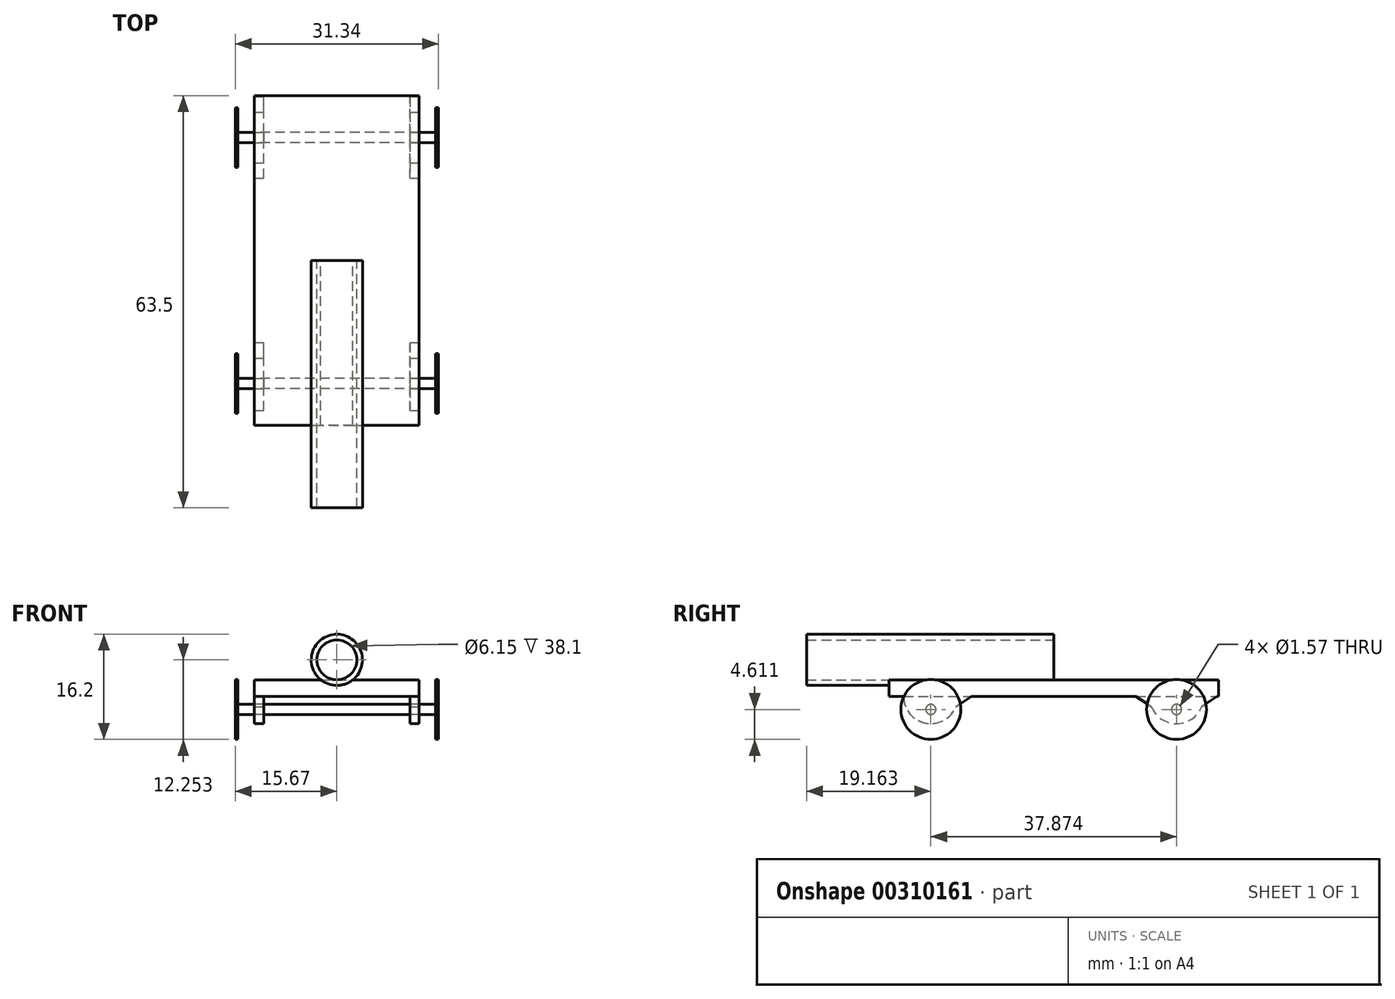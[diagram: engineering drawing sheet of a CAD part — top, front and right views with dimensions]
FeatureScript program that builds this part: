
annotation { "Feature Type Name" : "Feature", "Feature Type Description" : "" }
export const myFeature = defineFeature(function(context is Context, id is Id, definition is map)
    precondition{}
    {
        {
            var Q0;
            Q0=qCreatedBy(makeId("Top.planeOp"),FACE);
            var sketch = newSketch(context, id + "F0", { "sketchPlane" : qUnion([Q0])});
            skLineSegment(sketch, "E0", {"start": v(-12.7, 25.4) * mm, "end": v(-12.7, -25.4) * mm});
            skLineSegment(sketch, "E1", {"start": v(-12.7, -25.4) * mm, "end": v(12.7, -25.4) * mm});
            skLineSegment(sketch, "E2", {"start": v(12.7, -25.4) * mm, "end": v(12.7, 25.4) * mm});
            skLineSegment(sketch, "E3", {"start": v(12.7, 25.4) * mm, "end": v(-12.7, 25.4) * mm});
            skLineSegment(sketch, "E4", {"start": v(0, 25.4) * mm, "end": v(0, -25.4) * mm, "construction": true});
            skSolve(sketch);
        }
        {
            var Q0;
            Q0=makeQuery(id+"F0.imprint","IMPRINT",FACE,{"disambiguationData":[TD([[makeQuery(id+"F0.imprint","IMPRINT",EDGE,{"derivedFrom":sQuery(id+"F0.wireOp",EDGE,"E0")}),1.0]])]});
            extrude(context, id + "F1", {"entities" : qUnion([Q0]), "depth" : 2.54 * mm});
        }
        {
            var Q0;
            Q0=makeQuery(id+"F1.opExtrude","SWEPT_FACE",FACE,{"disambiguationData":[OSD([sQuery(id+"F0.wireOp",EDGE,"E1")])]});
            var sketch = newSketch(context, id + "F2", { "sketchPlane" : qUnion([Q0])});
            skCircle(sketch, "E5", {"center": v(0, 5.61) * mm, "radius": 3.07 * mm});
            skCircle(sketch, "E6", {"center": v(0, 5.61) * mm, "radius": 3.95 * mm});
            skSolve(sketch);
        }
        {
            var Q0;
            {var subQ0=sQuery(id+"F2.wireOp",EDGE,"E5");Q0=makeQuery(id+"F2.imprint","IMPRINT",FACE,{"disambiguationData":[TD([[makeQuery(id+"F2.imprint","IMPRINT",EDGE,{"derivedFrom":subQ0}),-1.0]])]});}
            var Q1;
            {var subQ0=sQuery(id+"F2.wireOp",EDGE,"E6");var subQ1=makeQuery(id+"F1.opExtrude","CAP_EDGE",EDGE,{"disambiguationData":[OSD([sQuery(id+"F0.wireOp",EDGE,"E1")])],"isStart":false});var subQ2=makeQuery(id+"F2.imprint","INTERSECT",VERTEX,{"disambiguationData":[OD(0.0)],"derivedFrom":[subQ1,subQ0]});Q1=makeQuery(id+"F2.imprint","IMPRINT",FACE,{"disambiguationData":[TD([[makeQuery(id+"F2.imprint","IMPRINT",EDGE,{"disambiguationData":[TD([[subQ2,-1.0]])],"derivedFrom":subQ0}),1.0]])]});}
            extrude(context, id + "F3", {"entities" : qUnion([Q0, Q1]), "operationType" : NewBodyOperationType.ADD, "depth" : 12.7 * mm, "hasSecondDirection" : true, "secondDirectionOppositeDirection" : true, "secondDirectionDepth" : 25.4 * mm});
        }
        {
            var Q0;
            Q0=makeQuery(id+"F1.opExtrude","SWEPT_FACE",FACE,{"disambiguationData":[OSD([sQuery(id+"F0.wireOp",EDGE,"E2")])]});
            var sketch = newSketch(context, id + "F4", { "sketchPlane" : qUnion([Q0])});
            skCircle(sketch, "E7", {"center": v(-18.94, 0) * mm, "radius": 4.21 * mm});
            skCircle(sketch, "E8", {"center": v(18.94, 0) * mm, "radius": 4.21 * mm});
            skLineSegment(sketch, "E9", {"start": v(0, 0) * mm, "end": v(-18.94, 0) * mm, "construction": true});
            skLineSegment(sketch, "E10", {"start": v(0, 0) * mm, "end": v(18.94, 0) * mm, "construction": true});
            skCircle(sketch, "E11", {"center": v(-18.94, -2.03) * mm, "radius": 0.78 * mm});
            skCircle(sketch, "E12", {"center": v(18.94, -2.03) * mm, "radius": 0.78 * mm});
            skLineSegment(sketch, "E13", {"start": v(-18.94, 0) * mm, "end": v(-18.94, -2.03) * mm, "construction": true});
            skLineSegment(sketch, "E14", {"start": v(18.94, 0) * mm, "end": v(18.94, -2.03) * mm, "construction": true});
            skSolve(sketch);
        }
        {
            var Q0;
            {var subQ0=sQuery(id+"F4.wireOp",EDGE,"E7");var subQ1=makeQuery(id+"F1.opExtrude","CAP_EDGE",EDGE,{"disambiguationData":[OSD([sQuery(id+"F0.wireOp",EDGE,"E2")])],"isStart":true});var subQ2=makeQuery(id+"F4.imprint","INTERSECT",VERTEX,{"disambiguationData":[OD(0.0)],"derivedFrom":[subQ1,subQ0]});Q0=makeQuery(id+"F4.imprint","IMPRINT",FACE,{"disambiguationData":[TD([[makeQuery(id+"F4.imprint","IMPRINT",EDGE,{"disambiguationData":[TD([[subQ2,1.0]])],"derivedFrom":subQ0}),1.0]])]});}
            var Q1;
            {var subQ0=sQuery(id+"F4.wireOp",EDGE,"E8");var subQ1=makeQuery(id+"F1.opExtrude","CAP_EDGE",EDGE,{"disambiguationData":[OSD([sQuery(id+"F0.wireOp",EDGE,"E2")])],"isStart":true});var subQ2=makeQuery(id+"F4.imprint","INTERSECT",VERTEX,{"disambiguationData":[OD(0.0)],"derivedFrom":[subQ1,subQ0]});Q1=makeQuery(id+"F4.imprint","IMPRINT",FACE,{"disambiguationData":[TD([[makeQuery(id+"F4.imprint","IMPRINT",EDGE,{"disambiguationData":[TD([[subQ2,1.0]])],"derivedFrom":subQ0}),1.0]])]});}
            extrude(context, id + "F5", {"entities" : qUnion([Q0, Q1]), "operationType" : NewBodyOperationType.ADD, "oppositeDirection" : true, "depth" : 25.4 * mm});
        }
        {
            var Q0;
            Q0=makeQuery(id+"F1.opExtrude","SWEPT_FACE",FACE,{"disambiguationData":[OSD([sQuery(id+"F0.wireOp",EDGE,"E3")])]});
            var sketch = newSketch(context, id + "F6", { "sketchPlane" : qUnion([Q0])});
            skLineSegment(sketch, "E15", {"start": v(-11.27, 0) * mm, "end": v(0, 0) * mm});
            skLineSegment(sketch, "E16", {"start": v(0, 0) * mm, "end": v(11.27, 0) * mm});
            skLineSegment(sketch, "E17", {"start": v(11.27, 0) * mm, "end": v(11.27, -4.56) * mm});
            skLineSegment(sketch, "E18", {"start": v(11.27, -4.56) * mm, "end": v(-11.27, -4.56) * mm});
            skLineSegment(sketch, "E19", {"start": v(-11.27, -4.56) * mm, "end": v(-11.27, 0) * mm});
            skSolve(sketch);
        }
        {
            var Q0;
            Q0=makeQuery(id+"F6.imprint","IMPRINT",FACE,{"disambiguationData":[TD([[makeQuery(id+"F6.imprint","IMPRINT",EDGE,{"derivedFrom":sQuery(id+"F6.wireOp",EDGE,"E15")}),-1.0]])]});
            extrude(context, id + "F7", {"entities" : qUnion([Q0]), "operationType" : NewBodyOperationType.REMOVE, "oppositeDirection" : true, "depth" : 50.55 * mm});
        }
        {
            var Q0;
            Q0=makeQuery(id+"F4.imprint","IMPRINT",FACE,{"disambiguationData":[TD([[makeQuery(id+"F4.imprint","IMPRINT",EDGE,{"derivedFrom":sQuery(id+"F4.wireOp",EDGE,"E11")}),1.0]])]});
            var Q1;
            Q1=makeQuery(id+"F4.imprint","IMPRINT",FACE,{"disambiguationData":[TD([[makeQuery(id+"F4.imprint","IMPRINT",EDGE,{"derivedFrom":sQuery(id+"F4.wireOp",EDGE,"E12")}),1.0]])]});
            extrude(context, id + "F8", {"entities" : qUnion([Q0, Q1]), "depth" : 2.54 * mm, "hasSecondDirection" : true, "secondDirectionOppositeDirection" : true, "secondDirectionDepth" : 27.94 * mm});
        }
        {
            var Q0;
            Q0=makeQuery(id+"F8.opExtrude","CAP_FACE",FACE,{"disambiguationData":[OSD([sQuery(id+"F4.wireOp",EDGE,"E11")])],"isStart":false});
            var sketch = newSketch(context, id + "F9", { "sketchPlane" : qUnion([Q0])});
            skCircle(sketch, "E20", {"center": v(-18.94, -2.03) * mm, "radius": 4.61 * mm});
            skCircle(sketch, "E21", {"center": v(18.94, -2.03) * mm, "radius": 4.61 * mm});
            skSolve(sketch);
        }
        {
            var Q0;
            Q0 = qSketchRegion(id + "F9", true);
            extrude(context, id + "F10", {"entities" : qUnion([Q0]), "operationType" : NewBodyOperationType.ADD, "depth" : 0.43 * mm});
        }
        {
            var Q0;
            Q0=makeQuery(id+"F8.opExtrude","CAP_FACE",FACE,{"disambiguationData":[OSD([sQuery(id+"F4.wireOp",EDGE,"E12")])],"isStart":true});
            var sketch = newSketch(context, id + "F11", { "sketchPlane" : qUnion([Q0])});
            skCircle(sketch, "E22", {"center": v(-18.94, -2.03) * mm, "radius": 4.61 * mm});
            skCircle(sketch, "E23", {"center": v(18.94, -2.03) * mm, "radius": 4.61 * mm});
            skSolve(sketch);
        }
        {
            var Q0;
            Q0=makeQuery(id+"F11.imprint","IMPRINT",FACE,{"disambiguationData":[TD([[makeQuery(id+"F11.imprint","IMPRINT",EDGE,{"derivedFrom":sQuery(id+"F11.wireOp",EDGE,"E22")}),1.0]])]});
            var Q1;
            Q1=makeQuery(id+"F11.imprint","IMPRINT",FACE,{"disambiguationData":[TD([[makeQuery(id+"F11.imprint","IMPRINT",EDGE,{"derivedFrom":makeQuery(id+"F8.opExtrude","CAP_EDGE",EDGE,{"disambiguationData":[OSD([sQuery(id+"F4.wireOp",EDGE,"E12")])],"isStart":true})}),-1.0]])]});
            var Q2;
            Q2=makeQuery(id+"F11.imprint","IMPRINT",FACE,{"disambiguationData":[TD([[makeQuery(id+"F11.imprint","IMPRINT",EDGE,{"derivedFrom":sQuery(id+"F11.wireOp",EDGE,"E23")}),1.0]])]});
            extrude(context, id + "F12", {"entities" : qUnion([Q0, Q1, Q2]), "operationType" : NewBodyOperationType.ADD, "depth" : 0.43 * mm});
        }
        {
            var Q0;
            {var subQ0=sQuery(id+"F4.wireOp",EDGE,"E8");var subQ1=sQuery(id+"F0.wireOp",EDGE,"E2");Q0=makeQuery(id+"F7.boolean.opBoolean","SPLIT",EDGE,{"disambiguationData":[TD([makeQuery(id+"F1.opExtrude","SWEPT_FACE",FACE,{"disambiguationData":[OSD([subQ1])]})])],"derivedFrom":makeQuery(id+"F5.opExtrude","SWEPT_EDGE",EDGE,{"disambiguationData":[OSD([subQ1,subQ0]),TDD([makeQuery(id+"F4.imprint","INTERSECT",VERTEX,{"disambiguationData":[OD(0.0)],"derivedFrom":[makeQuery(id+"F1.opExtrude","CAP_EDGE",EDGE,{"disambiguationData":[OSD([subQ1])],"isStart":true}),subQ0]})])]})});}
            var Q1;
            {var subQ0=sQuery(id+"F4.wireOp",EDGE,"E8");var subQ1=sQuery(id+"F0.wireOp",EDGE,"E2");Q1=makeQuery(id+"F7.boolean.opBoolean","SPLIT",EDGE,{"disambiguationData":[TD([makeQuery(id+"F1.opExtrude","SWEPT_FACE",FACE,{"disambiguationData":[OSD([subQ1])]})])],"derivedFrom":makeQuery(id+"F5.opExtrude","SWEPT_EDGE",EDGE,{"disambiguationData":[OSD([subQ1,subQ0]),TDD([makeQuery(id+"F4.imprint","INTERSECT",VERTEX,{"disambiguationData":[OD(1.0)],"derivedFrom":[makeQuery(id+"F1.opExtrude","CAP_EDGE",EDGE,{"disambiguationData":[OSD([subQ1])],"isStart":true}),subQ0]})])]})});}
            var Q2;
            {var subQ0=sQuery(id+"F0.wireOp",EDGE,"E2");var subQ1=sQuery(id+"F0.wireOp",EDGE,"E0");var subQ2=sQuery(id+"F4.wireOp",EDGE,"E8");Q2=makeQuery(id+"F7.boolean.opBoolean","SPLIT",EDGE,{"disambiguationData":[TD([makeQuery(id+"F1.opExtrude","SWEPT_FACE",FACE,{"disambiguationData":[OSD([subQ1])]})])],"derivedFrom":makeQuery(id+"F5.opExtrude","SWEPT_EDGE",EDGE,{"disambiguationData":[OSD([subQ0,subQ2]),TDD([makeQuery(id+"F4.imprint","INTERSECT",VERTEX,{"disambiguationData":[OD(1.0)],"derivedFrom":[makeQuery(id+"F1.opExtrude","CAP_EDGE",EDGE,{"disambiguationData":[OSD([subQ0])],"isStart":true}),subQ2]})])]})});}
            var Q3;
            {var subQ0=sQuery(id+"F0.wireOp",EDGE,"E2");var subQ1=sQuery(id+"F0.wireOp",EDGE,"E0");var subQ2=sQuery(id+"F4.wireOp",EDGE,"E8");Q3=makeQuery(id+"F7.boolean.opBoolean","SPLIT",EDGE,{"disambiguationData":[TD([makeQuery(id+"F1.opExtrude","SWEPT_FACE",FACE,{"disambiguationData":[OSD([subQ1])]})])],"derivedFrom":makeQuery(id+"F5.opExtrude","SWEPT_EDGE",EDGE,{"disambiguationData":[OSD([subQ0,subQ2]),TDD([makeQuery(id+"F4.imprint","INTERSECT",VERTEX,{"disambiguationData":[OD(0.0)],"derivedFrom":[makeQuery(id+"F1.opExtrude","CAP_EDGE",EDGE,{"disambiguationData":[OSD([subQ0])],"isStart":true}),subQ2]})])]})});}
            var Q4;
            {var subQ0=sQuery(id+"F4.wireOp",EDGE,"E7");var subQ1=sQuery(id+"F0.wireOp",EDGE,"E2");var subQ2=sQuery(id+"F0.wireOp",EDGE,"E0");Q4=makeQuery(id+"F7.boolean.opBoolean","SPLIT",EDGE,{"disambiguationData":[TD([makeQuery(id+"F1.opExtrude","SWEPT_FACE",FACE,{"disambiguationData":[OSD([subQ2])]})])],"derivedFrom":makeQuery(id+"F5.opExtrude","SWEPT_EDGE",EDGE,{"disambiguationData":[OSD([subQ1,subQ0]),TDD([makeQuery(id+"F4.imprint","INTERSECT",VERTEX,{"disambiguationData":[OD(1.0)],"derivedFrom":[makeQuery(id+"F1.opExtrude","CAP_EDGE",EDGE,{"disambiguationData":[OSD([subQ1])],"isStart":true}),subQ0]})])]})});}
            var Q5;
            {var subQ0=sQuery(id+"F4.wireOp",EDGE,"E7");var subQ1=sQuery(id+"F0.wireOp",EDGE,"E2");var subQ2=sQuery(id+"F0.wireOp",EDGE,"E0");Q5=makeQuery(id+"F7.boolean.opBoolean","SPLIT",EDGE,{"disambiguationData":[TD([makeQuery(id+"F1.opExtrude","SWEPT_FACE",FACE,{"disambiguationData":[OSD([subQ2])]})])],"derivedFrom":makeQuery(id+"F5.opExtrude","SWEPT_EDGE",EDGE,{"disambiguationData":[OSD([subQ1,subQ0]),TDD([makeQuery(id+"F4.imprint","INTERSECT",VERTEX,{"disambiguationData":[OD(0.0)],"derivedFrom":[makeQuery(id+"F1.opExtrude","CAP_EDGE",EDGE,{"disambiguationData":[OSD([subQ1])],"isStart":true}),subQ0]})])]})});}
            var Q6;
            {var subQ0=sQuery(id+"F4.wireOp",EDGE,"E7");var subQ1=sQuery(id+"F0.wireOp",EDGE,"E2");Q6=makeQuery(id+"F7.boolean.opBoolean","SPLIT",EDGE,{"disambiguationData":[TD([makeQuery(id+"F1.opExtrude","SWEPT_FACE",FACE,{"disambiguationData":[OSD([subQ1])]})])],"derivedFrom":makeQuery(id+"F5.opExtrude","SWEPT_EDGE",EDGE,{"disambiguationData":[OSD([subQ1,subQ0]),TDD([makeQuery(id+"F4.imprint","INTERSECT",VERTEX,{"disambiguationData":[OD(0.0)],"derivedFrom":[makeQuery(id+"F1.opExtrude","CAP_EDGE",EDGE,{"disambiguationData":[OSD([subQ1])],"isStart":true}),subQ0]})])]})});}
            var Q7;
            {var subQ0=sQuery(id+"F4.wireOp",EDGE,"E7");var subQ1=sQuery(id+"F0.wireOp",EDGE,"E2");Q7=makeQuery(id+"F7.boolean.opBoolean","SPLIT",EDGE,{"disambiguationData":[TD([makeQuery(id+"F1.opExtrude","SWEPT_FACE",FACE,{"disambiguationData":[OSD([subQ1])]})])],"derivedFrom":makeQuery(id+"F5.opExtrude","SWEPT_EDGE",EDGE,{"disambiguationData":[OSD([subQ1,subQ0]),TDD([makeQuery(id+"F4.imprint","INTERSECT",VERTEX,{"disambiguationData":[OD(1.0)],"derivedFrom":[makeQuery(id+"F1.opExtrude","CAP_EDGE",EDGE,{"disambiguationData":[OSD([subQ1])],"isStart":true}),subQ0]})])]})});}
            chamfer(context, id + "F13", {"entities" : qUnion([Q0, Q1, Q2, Q3, Q4, Q5, Q6, Q7]), "width" : 2.54 * mm, "tangentPropagation" : true});
        }
    });
